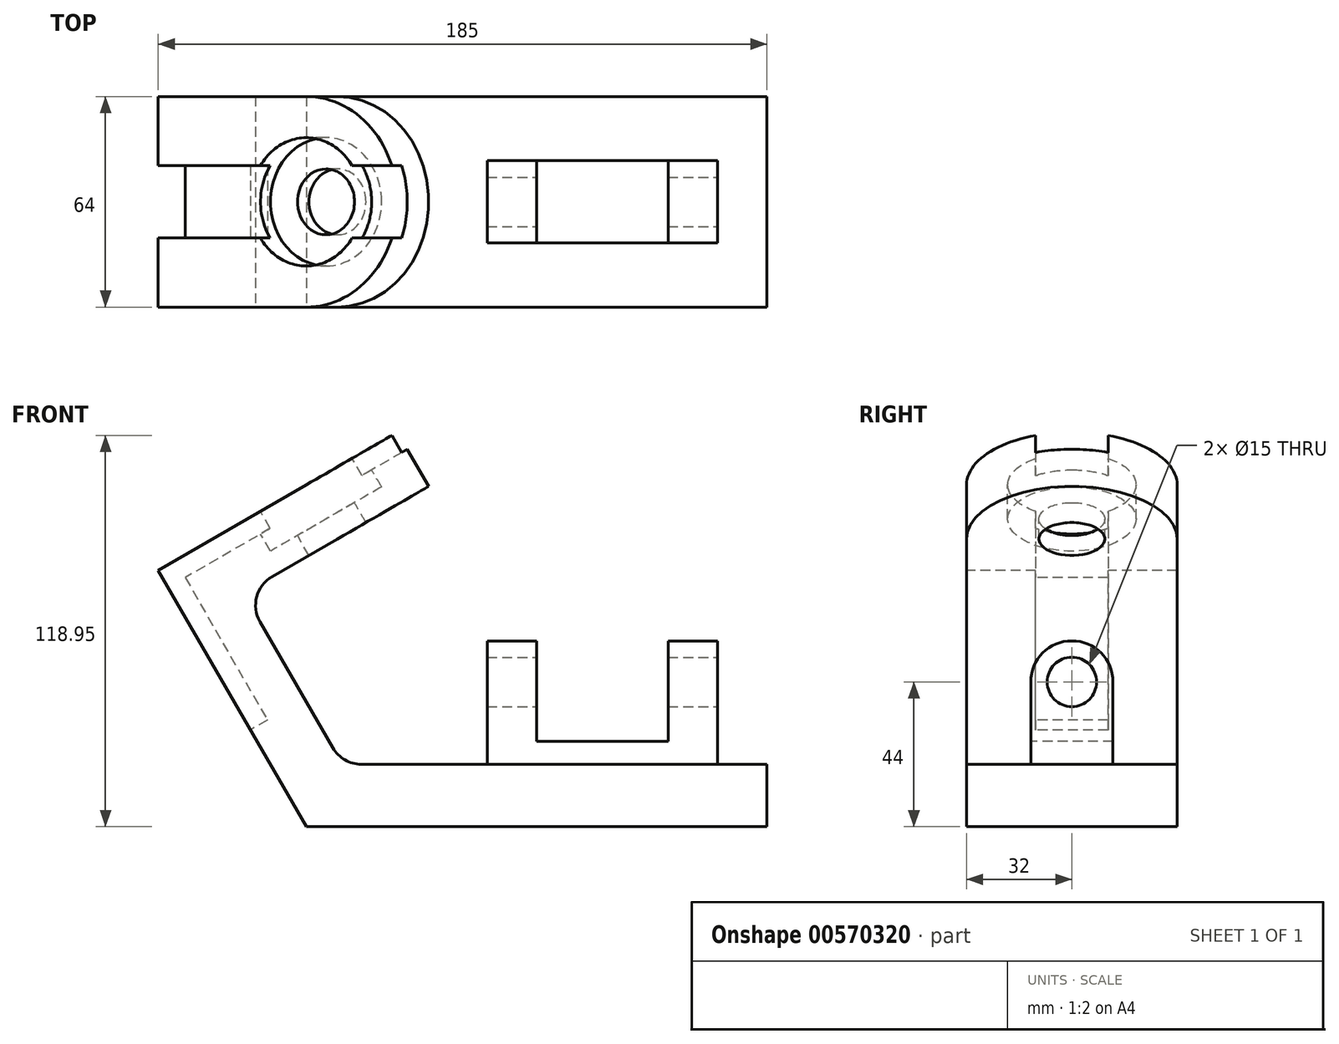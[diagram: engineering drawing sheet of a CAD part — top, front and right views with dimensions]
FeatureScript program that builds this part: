
annotation { "Feature Type Name" : "Feature", "Feature Type Description" : "" }
export const myFeature = defineFeature(function(context is Context, id is Id, definition is map)
    precondition{}
    {
        {
            var Q0;
            Q0=qCreatedBy(makeId("Front.planeOp"),FACE);
            var sketch = newSketch(context, id + "F0", { "sketchPlane" : qUnion([Q0])});
            skLineSegment(sketch, "E0", {"start": v(0, 0) * mm, "end": v(140, 0) * mm});
            skLineSegment(sketch, "E1", {"start": v(140, 0) * mm, "end": v(140, 19) * mm});
            skLineSegment(sketch, "E2", {"start": v(0, 0) * mm, "end": v(-45, 77.94) * mm});
            skLineSegment(sketch, "E3", {"start": v(-45, 77.94) * mm, "end": v(0, 103.92) * mm});
            skLineSegment(sketch, "E4", {"start": v(0, 103.92) * mm, "end": v(9.5, 87.47) * mm});
            skLineSegment(sketch, "E5", {"start": v(9.5, 87.47) * mm, "end": v(-10.39, 75.99) * mm});
            skLineSegment(sketch, "E6", {"start": v(140, 19) * mm, "end": v(16.74, 19) * mm});
            skLineSegment(sketch, "E7.0", {"start": v(8.08, 24) * mm, "end": v(-14.05, 62.33) * mm});
            skPoint(sketch, "E8.visualSharp", {"position": v(-19.05, 70.99) * mm});
            skArc(sketch, "E8.filletArc", {"start": v(-10.39, 75.99) * mm, "mid": v(-15.04, 69.92) * mm, "end": v(-14.05, 62.33) * mm});
            skPoint(sketch, "E9.visualSharp", {"position": v(10.97, 19) * mm});
            skArc(sketch, "E9.filletArc", {"start": v(8.08, 24) * mm, "mid": v(11.74, 20.34) * mm, "end": v(16.74, 19) * mm});
            skSolve(sketch);
        }
        {
            var Q0;
            Q0 = qSketchRegion(id + "F0", true);
            extrude(context, id + "F1", {"entities" : qUnion([Q0]), "oppositeDirection" : true, "depth" : 64 * mm, "offsetDistance" : 25 * mm});
        }
        {
            var Q0;
            Q0=makeQuery(id+"F1.opExtrude","SWEPT_FACE",FACE,{"disambiguationData":[OSD([sQuery(id+"F0.wireOp",EDGE,"E3")])]});
            var sketch = newSketch(context, id + "F2", { "sketchPlane" : qUnion([Q0])});
            skArc(sketch, "E10", {"start": v(51.96, 0) * mm, "mid": v(83.96, 32) * mm, "end": v(51.96, 64) * mm});
            skLineSegment(sketch, "E11", {"start": v(51.96, 64) * mm, "end": v(51.96, 0) * mm});
            skSolve(sketch);
        }
        {
            var Q0;
            Q0 = qSketchRegion(id + "F2", true);
            extrude(context, id + "F3", {"entities" : qUnion([Q0]), "operationType" : NewBodyOperationType.ADD, "oppositeDirection" : true, "depth" : 19 * mm, "offsetDistance" : 25 * mm});
        }
        {
            var Q0;
            Q0=makeQuery(id+"F3.boolean.opBoolean","MERGE",FACE,{"derivedFrom":[makeQuery(id+"F1.opExtrude","SWEPT_FACE",FACE,{"disambiguationData":[OSD([sQuery(id+"F0.wireOp",EDGE,"E3")])]}),makeQuery(id+"F3.opExtrude","CAP_FACE",FACE,{"disambiguationData":[OSD([sQuery(id+"F2.wireOp",EDGE,"E10"),sQuery(id+"F2.wireOp",EDGE,"E11")])],"isStart":true})]});
            var sketch = newSketch(context, id + "F4", { "sketchPlane" : qUnion([Q0])});
            skCircle(sketch, "E12", {"center": v(51.96, 32) * mm, "radius": 10 * mm});
            skSolve(sketch);
        }
        {
            var Q0;
            Q0 = qSketchRegion(id + "F4", true);
            extrude(context, id + "F5", {"entities" : qUnion([Q0]), "operationType" : NewBodyOperationType.REMOVE, "oppositeDirection" : true, "depth" : 19 * mm, "offsetDistance" : 25 * mm});
        }
        {
            var Q0;
            Q0=makeQuery(id+"F3.boolean.opBoolean","MERGE",FACE,{"derivedFrom":[makeQuery(id+"F1.opExtrude","SWEPT_FACE",FACE,{"disambiguationData":[OSD([sQuery(id+"F0.wireOp",EDGE,"E3")])]}),makeQuery(id+"F3.opExtrude","CAP_FACE",FACE,{"disambiguationData":[OSD([sQuery(id+"F2.wireOp",EDGE,"E10"),sQuery(id+"F2.wireOp",EDGE,"E11")])],"isStart":true})]});
            var sketch = newSketch(context, id + "F6", { "sketchPlane" : qUnion([Q0])});
            skCircle(sketch, "E13", {"center": v(51.96, 32) * mm, "radius": 19.5 * mm});
            skSolve(sketch);
        }
        {
            var Q0;
            Q0 = qSketchRegion(id + "F6", true);
            extrude(context, id + "F7", {"entities" : qUnion([Q0]), "operationType" : NewBodyOperationType.REMOVE, "oppositeDirection" : true, "depth" : 12 * mm, "offsetDistance" : 25 * mm});
        }
        {
            var Q0;
            Q0=makeQuery(id+"F3.boolean.opBoolean","MERGE",FACE,{"derivedFrom":[makeQuery(id+"F1.opExtrude","SWEPT_FACE",FACE,{"disambiguationData":[OSD([sQuery(id+"F0.wireOp",EDGE,"E3")])]}),makeQuery(id+"F3.opExtrude","CAP_FACE",FACE,{"disambiguationData":[OSD([sQuery(id+"F2.wireOp",EDGE,"E10"),sQuery(id+"F2.wireOp",EDGE,"E11")])],"isStart":true})]});
            var sketch = newSketch(context, id + "F8", { "sketchPlane" : qUnion([Q0])});
            skLineSegment(sketch, "E14", {"start": v(83.96, 32) * mm, "end": v(0, 32) * mm, "construction": true});
            skLineSegment(sketch, "E15.0", {"start": v(83.96, 43) * mm, "end": v(0, 43) * mm});
            skLineSegment(sketch, "E16.0", {"start": v(83.96, 21) * mm, "end": v(0, 21) * mm});
            skLineSegment(sketch, "E17", {"start": v(83.96, 43) * mm, "end": v(83.96, 21) * mm});
            skLineSegment(sketch, "E18", {"start": v(0, 43) * mm, "end": v(0, 21) * mm});
            skSolve(sketch);
        }
        {
            var Q0;
            Q0 = qSketchRegion(id + "F8", true);
            extrude(context, id + "F9", {"entities" : qUnion([Q0]), "operationType" : NewBodyOperationType.REMOVE, "oppositeDirection" : true, "depth" : 6 * mm, "offsetDistance" : 25 * mm});
        }
        {
            var Q0;
            Q0=makeQuery(id+"F1.opExtrude","SWEPT_FACE",FACE,{"disambiguationData":[OSD([sQuery(id+"F0.wireOp",EDGE,"E2")])]});
            var sketch = newSketch(context, id + "F10", { "sketchPlane" : qUnion([Q0])});
            skLineSegment(sketch, "E19", {"start": v(-43, 90) * mm, "end": v(-43, 34) * mm});
            skLineSegment(sketch, "E20", {"start": v(-43, 34) * mm, "end": v(-21, 34) * mm});
            skLineSegment(sketch, "E21", {"start": v(-21, 34) * mm, "end": v(-21, 90) * mm});
            skLineSegment(sketch, "E22", {"start": v(-21, 90) * mm, "end": v(-43, 90) * mm});
            skSolve(sketch);
        }
        {
            var Q0;
            Q0 = qSketchRegion(id + "F10", true);
            extrude(context, id + "F11", {"entities" : qUnion([Q0]), "operationType" : NewBodyOperationType.REMOVE, "oppositeDirection" : true, "depth" : 6 * mm, "offsetDistance" : 25 * mm});
        }
        {
            var Q0;
            Q0=makeQuery(id+"F1.opExtrude","SWEPT_FACE",FACE,{"disambiguationData":[OSD([sQuery(id+"F0.wireOp",EDGE,"E6")])]});
            var sketch = newSketch(context, id + "F12", { "sketchPlane" : qUnion([Q0])});
            skLineSegment(sketch, "E23.0", {"start": v(125, 44.5) * mm, "end": v(55, 44.5) * mm});
            skLineSegment(sketch, "E24.0", {"start": v(125, 19.5) * mm, "end": v(55, 19.5) * mm});
            skPoint(sketch, "E25.orphan", {"position": v(140, 32) * mm});
            skLineSegment(sketch, "E26", {"start": v(125, 44.5) * mm, "end": v(125, 19.5) * mm});
            skLineSegment(sketch, "E27", {"start": v(55, 44.5) * mm, "end": v(55, 19.5) * mm});
            skSolve(sketch);
        }
        {
            var Q0;
            Q0 = qSketchRegion(id + "F12", true);
            extrude(context, id + "F13", {"entities" : qUnion([Q0]), "operationType" : NewBodyOperationType.ADD, "depth" : 25 * mm, "offsetDistance" : 25 * mm});
        }
        {
            var Q0;
            Q0=makeQuery(id+"F13.opExtrude","SWEPT_FACE",FACE,{"disambiguationData":[OSD([sQuery(id+"F12.wireOp",EDGE,"E26")])]});
            var sketch = newSketch(context, id + "F14", { "sketchPlane" : qUnion([Q0])});
            skArc(sketch, "E28", {"start": v(44.5, 44) * mm, "mid": v(32, 56.5) * mm, "end": v(19.5, 44) * mm});
            skLineSegment(sketch, "E29", {"start": v(19.5, 44) * mm, "end": v(44.5, 44) * mm});
            skSolve(sketch);
        }
        {
            var Q0;
            Q0 = qSketchRegion(id + "F14", true);
            extrude(context, id + "F15", {"entities" : qUnion([Q0]), "operationType" : NewBodyOperationType.ADD, "oppositeDirection" : true, "depth" : 70 * mm, "offsetDistance" : 25 * mm});
        }
        {
            var Q0;
            Q0=makeQuery(id+"F15.boolean.opBoolean","MERGE",FACE,{"derivedFrom":[makeQuery(id+"F13.opExtrude","SWEPT_FACE",FACE,{"disambiguationData":[OSD([sQuery(id+"F12.wireOp",EDGE,"E26")])]}),makeQuery(id+"F15.opExtrude","CAP_FACE",FACE,{"disambiguationData":[OSD([sQuery(id+"F14.wireOp",EDGE,"E28"),sQuery(id+"F14.wireOp",EDGE,"E29")])],"isStart":true})]});
            var sketch = newSketch(context, id + "F16", { "sketchPlane" : qUnion([Q0])});
            skCircle(sketch, "E30", {"center": v(32, 44) * mm, "radius": 7.5 * mm});
            skSolve(sketch);
        }
        {
            var Q0;
            Q0 = qSketchRegion(id + "F16", true);
            extrude(context, id + "F17", {"entities" : qUnion([Q0]), "operationType" : NewBodyOperationType.REMOVE, "oppositeDirection" : true, "depth" : 70 * mm, "offsetDistance" : 25 * mm});
        }
        {
            var Q0;
            Q0=makeQuery(id+"F13.opExtrude","SWEPT_FACE",FACE,{"disambiguationData":[OSD([sQuery(id+"F12.wireOp",EDGE,"E24.0")])]});
            var sketch = newSketch(context, id + "F18", { "sketchPlane" : qUnion([Q0])});
            skLineSegment(sketch, "E31", {"start": v(110, 26) * mm, "end": v(110, 66.12) * mm});
            skLineSegment(sketch, "E32", {"start": v(110, 26) * mm, "end": v(70, 26) * mm});
            skLineSegment(sketch, "E33", {"start": v(70, 26) * mm, "end": v(70, 66.12) * mm});
            skLineSegment(sketch, "E34", {"start": v(70, 66.12) * mm, "end": v(110, 66.12) * mm});
            skSolve(sketch);
        }
        {
            var Q0;
            Q0 = qSketchRegion(id + "F18", true);
            extrude(context, id + "F19", {"entities" : qUnion([Q0]), "operationType" : NewBodyOperationType.REMOVE, "endBound" : BoundingType.THROUGH_ALL, "oppositeDirection" : true, "depth" : 25 * mm, "offsetDistance" : 25 * mm});
        }
    });
